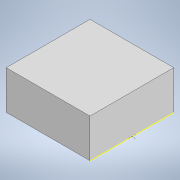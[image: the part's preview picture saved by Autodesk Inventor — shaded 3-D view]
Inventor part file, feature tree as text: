
AUTODESK INVENTOR PART (.ipt)
format: ipt  version: 2022 (Build 260153000, 153)  size: 108,032 bytes
history: native  units: in
note: dims shown in document units (in); Inventor stores cm internally (conversion verified against a paired STEP export)
features: sketch x3, extrude x2
ambient origin geometry x8: Origin, YZ Plane, XZ Plane, XY Plane, X Axis, Y Axis, Z Axis, Center Point
bodies: Solid1 (feature_tree)
feature tree (5):
  extrude  "Extrusion1"  Depth=0.2165in
  extrude  "Extrusion2"  Depth=0.2559in
  sketch  "Sketch5"  dims[d8=0.0787in d9=0.0in d10=0.2559in d11=0.0394in d12=0.0in]
  sketch  "Sketch2"  dims[d2=0.2165in d3=0.2165in]
  sketch  "Sketch4"  dims[d6=0.2559in d7=0.2559in]
